# Revit family: Vents_TT PRO_2016_19.08
name_source: partatom
category: Оборудование
revit_build: Autodesk Revit 2016 (Build: 20160314_0715(x64)
units: mm (PartAtom-declared; Revit-internal decimal feet)

## family parameters
Всегда вертикально = Нет
На основе рабочей плоскости = Нет
Общий = Нет
При загрузке вырезать с полостями = Нет
Размер круглого соединителя = Использовать диаметр
Тип детали = Вставляется
Точка расчета площади = Нет

## types (7) — shared parameters
CAT0 = Да
CAT1 = Да
CAT2 = Да
Certification = by Manifacturer
EC motor = Нет
Ingress Protection Rating = IPX4
LL7 = 98 мм
Motor IP Rating = IPX4
R3 = 49 мм
RR4 = 12 мм
URL = https://ventilation-system.com
Variable Speed Drive = Нет
Voltage = 230 В
W = 500 мм
Группа модели = ТТ PRO
Изготовитель = VENTS
Описание = Inline mixed-flow fan
Угол = 60.00°

## per-type parameters (varying)
- TT PRO 160: Current.Max=0 А; Current.Min=0 А; D=160 мм; FlowMax=565.0 м³/ч; FlowMin=415.0 м³/ч; HH1=50 мм; HH2=49 мм; HH3=110 мм; L8=82 мм; LL1=145 мм; LL2=112 мм; LL3=69 мм; LL4=41 мм; LL6=43 мм; MC Product Code=ТТ PRO 160; Mass=3.25 кг; PC=134 мм; PE=115 мм; Power max=50 Вт; Power min=42 Вт; R1=79 мм; R2=110 мм; RR3=43 мм; Service Zone=160 мм; Service Zone 1=240 мм; Service Zone 2=289 мм; Sound Pressure Level at 3m  dBA (Min/Max)=32/44; WW1=70 мм; WW2=52 мм
- TT PRO 200: Current.Max=0 А; Current.Min=0 А; D=200 мм; FlowMax=1040.0 м³/ч; FlowMin=830.0 м³/ч; HH1=50 мм; HH2=49 мм; HH3=120 мм; L8=82 мм; LL1=148 мм; LL2=115 мм; LL3=70 мм; LL4=41 мм; LL6=43 мм; MC Product Code=ТТ PRO 200; Mass=3.95 кг; PC=131 мм; PE=130 мм; Power max=108 Вт; Power min=76 Вт; R1=100 мм; R2=120 мм; RR3=43 мм; Service Zone=170 мм; Service Zone 1=259 мм; Service Zone 2=296 мм; Sound Pressure Level at 3m  dBA (Min/Max)=39/45; WW1=70 мм; WW2=52 мм
- TT PRO 250: Current.Max=1 А; Current.Min=1 А; D=250 мм; FlowMax=1400.0 м³/ч; FlowMin=1110.0 м³/ч; HH1=50 мм; HH2=49 мм; HH3=144 мм; L8=108 мм; LL1=192 мм; LL2=150 мм; LL3=119 мм; LL4=54 мм; LL6=89 мм; MC Product Code=ТТ PRO 250; Mass=7.80 кг; PC=170 мм; PE=153 мм; Power max=177 Вт; Power min=125 Вт; R1=123 мм; R2=144 мм; RR3=50 мм; Service Zone=194 мм; Service Zone 1=307 мм; Service Zone 2=383 мм; Sound Pressure Level at 3m  dBA (Min/Max)=44/51; WW1=70 мм; WW2=72 мм
- TT PRO 315: Current.Max=1 А; Current.Min=1 А; D=315 мм; FlowMax=2050.0 м³/ч; FlowMin=1570.0 м³/ч; HH1=68 мм; HH2=132 мм; HH3=181 мм; L8=108 мм; LL1=223 мм; LL2=192 мм; LL3=155 мм; LL4=54 мм; LL6=118 мм; MC Product Code=ТТ PRO 315; Mass=11.95 кг; PC=208 мм; PE=200 мм; Power max=320 Вт; Power min=230 Вт; R1=155 мм; R2=181 мм; RR3=50 мм; Service Zone=231 мм; Service Zone 1=382 мм; Service Zone 2=445 мм; Sound Pressure Level at 3m  dBA (Min/Max)=41/52; WW1=100 мм; WW2=102 мм
- TT PRO 150: Current.Max=0 А; Current.Min=0 А; D=150 мм; FlowMax=565.0 м³/ч; FlowMin=415.0 м³/ч; HH1=68 мм; HH2=132 мм; HH3=110 мм; L8=108 мм; LL1=145 мм; LL2=112 мм; LL3=71 мм; LL4=54 мм; LL6=118 мм; MC Product Code=ТТ PRO 150; Mass=2.95 кг; PC=134 мм; PE=113 мм; Power max=50 Вт; Power min=42 Вт; R1=74 мм; R2=110 мм; RR3=50 мм; Service Zone=160 мм; Service Zone 1=240 мм; Service Zone 2=289 мм; Sound Pressure Level at 3m  dBA (Min/Max)=32/44; WW1=56 мм; WW2=58 мм
- TT PRO 125: Current.Max=0 А; Current.Min=0 А; D=125 мм; FlowMax=350.0 м³/ч; FlowMin=240.0 м³/ч; HH1=50 мм; HH2=49 мм; HH3=98 мм; L8=82 мм; LL1=129 мм; LL2=100 мм; LL3=67 мм; LL4=41 мм; LL6=43 мм; MC Product Code=ТТ PRO 125; Mass=2.15 кг; PC=123 мм; PE=103 мм; Power max=29 Вт; Power min=25 Вт; R1=62 мм; R2=98 мм; RR3=31 мм; Service Zone=148 мм; Service Zone 1=216 мм; Service Zone 2=259 мм; Sound Pressure Level at 3m  dBA (Min/Max)=29/34; WW1=50 мм; WW2=52 мм
- TT PRO 100: Current.Max=0 А; Current.Min=0 А; D=100 мм; FlowMax=245.0 м³/ч; FlowMin=180.0 м³/ч; HH1=50 мм; HH2=49 мм; HH3=98 мм; L8=82 мм; LL1=151 мм; LL2=120 мм; LL3=65 мм; LL4=41 мм; LL6=43 мм; MC Product Code=ТТ PRO 100; Mass=1.75 кг; PC=123 мм; PE=103 мм; Power max=25 Вт; Power min=23 Вт; R1=49 мм; R2=98 мм; RR3=31 мм; Service Zone=148 мм; Service Zone 1=216 мм; Service Zone 2=303 мм; Sound Pressure Level at 3m  dBA (Min/Max)=27/32; WW1=50 мм; WW2=52 мм

## geometry (parser evidence)
native form markers: Blend x4, Sweep x2
no freeform markers — native parametric forms only
